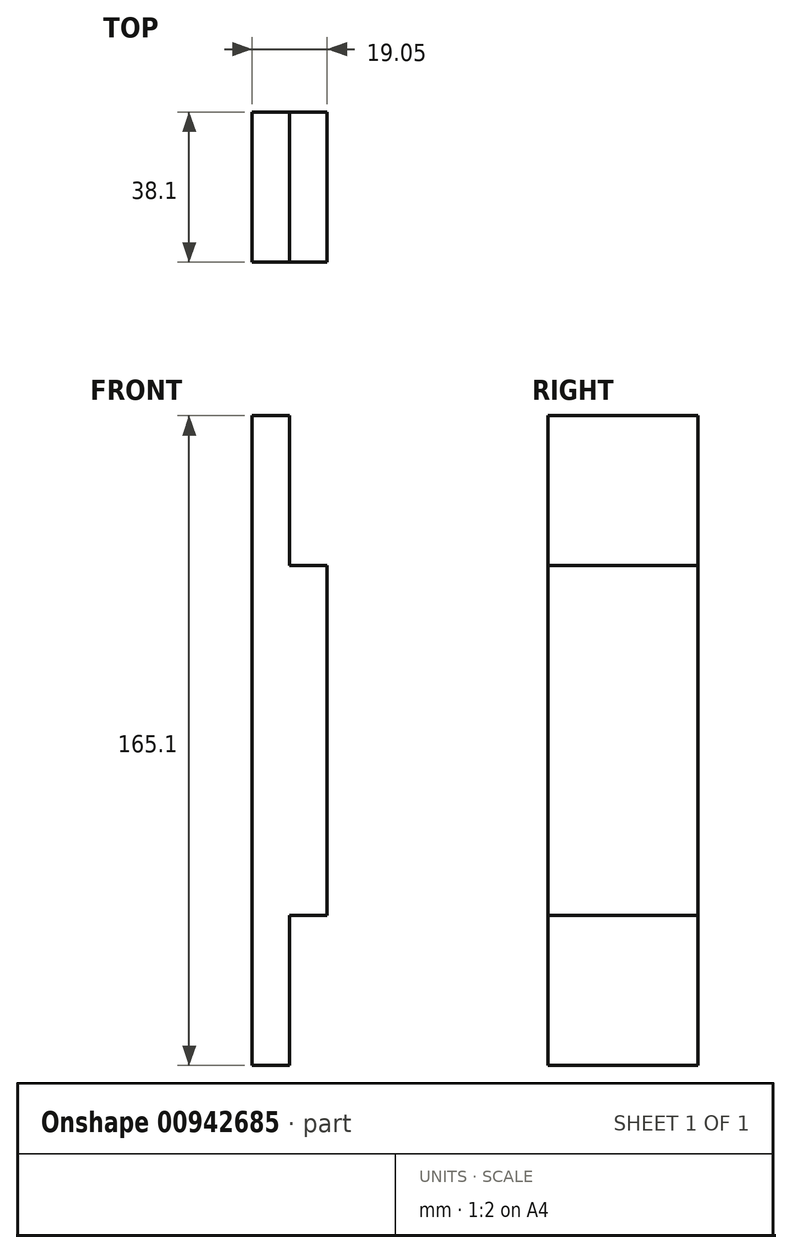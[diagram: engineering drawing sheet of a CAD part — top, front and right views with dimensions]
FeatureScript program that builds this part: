
annotation { "Feature Type Name" : "Feature", "Feature Type Description" : "" }
export const myFeature = defineFeature(function(context is Context, id is Id, definition is map)
    precondition{}
    {
        {
            var Q0;
            Q0=qCreatedBy(makeId("Right.planeOp"),FACE);
            var sketch = newSketch(context, id + "F0", { "sketchPlane" : qUnion([Q0])});
            skLineSegment(sketch, "E0.bottom", {"start": v(-0.95, -36.64) * mm, "end": v(-39.05, -36.64) * mm});
            skLineSegment(sketch, "E0.top", {"start": v(-0.95, 128.46) * mm, "end": v(-39.05, 128.46) * mm});
            skLineSegment(sketch, "E0.left", {"start": v(-0.95, -36.64) * mm, "end": v(-0.95, 128.46) * mm});
            skLineSegment(sketch, "E0.right", {"start": v(-39.05, -36.64) * mm, "end": v(-39.05, 128.46) * mm});
            skPoint(sketch, "E0.middle", {"position": v(-20, 45.91) * mm});
            skSolve(sketch);
        }
        {
            var Q0;
            Q0 = qSketchRegion(id + "F0", true);
            extrude(context, id + "F1", {"entities" : qUnion([Q0]), "depth" : 19.05 * mm, "offsetDistance" : 25.4 * mm});
        }
        {
            var Q0;
            Q0=makeQuery(id+"F1.opExtrude","CAP_FACE",FACE,{"disambiguationData":[OSD([sQuery(id+"F0.wireOp",EDGE,"E0.bottom"),sQuery(id+"F0.wireOp",EDGE,"E0.top"),sQuery(id+"F0.wireOp",EDGE,"E0.left"),sQuery(id+"F0.wireOp",EDGE,"E0.right")])],"isStart":false});
            var sketch = newSketch(context, id + "F2", { "sketchPlane" : qUnion([Q0])});
            skLineSegment(sketch, "E1.bottom", {"start": v(-39.05, 128.46) * mm, "end": v(-0.95, 128.46) * mm});
            skLineSegment(sketch, "E1.top", {"start": v(-39.05, 90.36) * mm, "end": v(-0.95, 90.36) * mm});
            skLineSegment(sketch, "E1.left", {"start": v(-39.05, 128.46) * mm, "end": v(-39.05, 90.36) * mm});
            skLineSegment(sketch, "E1.right", {"start": v(-0.95, 128.46) * mm, "end": v(-0.95, 90.36) * mm});
            skLineSegment(sketch, "E2.bottom", {"start": v(-0.95, -36.64) * mm, "end": v(-39.05, -36.64) * mm});
            skLineSegment(sketch, "E2.top", {"start": v(-0.95, 1.46) * mm, "end": v(-39.05, 1.46) * mm});
            skLineSegment(sketch, "E2.left", {"start": v(-0.95, -36.64) * mm, "end": v(-0.95, 1.46) * mm});
            skLineSegment(sketch, "E2.right", {"start": v(-39.05, -36.64) * mm, "end": v(-39.05, 1.46) * mm});
            skSolve(sketch);
        }
        {
            var Q0;
            Q0=makeQuery(id+"F2.imprint","IMPRINT",FACE,{"disambiguationData":[TD([[makeQuery(id+"F2.imprint","IMPRINT",EDGE,{"derivedFrom":sQuery(id+"F2.wireOp",EDGE,"E1.bottom")}),1.0]])]});
            var Q1;
            Q1=makeQuery(id+"F2.imprint","IMPRINT",FACE,{"disambiguationData":[TD([[makeQuery(id+"F2.imprint","IMPRINT",EDGE,{"derivedFrom":sQuery(id+"F2.wireOp",EDGE,"E2.bottom")}),-1.0]])]});
            extrude(context, id + "F3", {"entities" : qUnion([Q0, Q1]), "operationType" : NewBodyOperationType.REMOVE, "oppositeDirection" : true, "depth" : 9.52 * mm, "offsetDistance" : 25.4 * mm});
        }
    });
